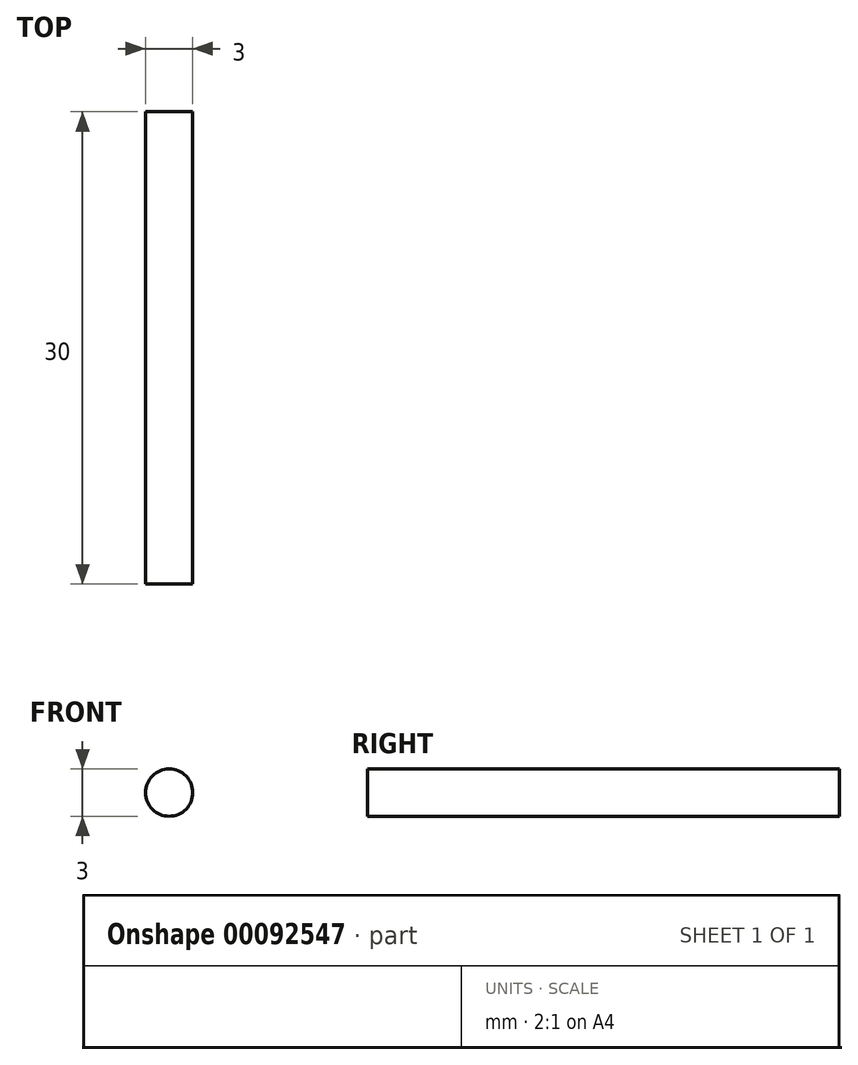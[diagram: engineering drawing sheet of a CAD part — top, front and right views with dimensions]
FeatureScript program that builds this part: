
annotation { "Feature Type Name" : "Feature", "Feature Type Description" : "" }
export const myFeature = defineFeature(function(context is Context, id is Id, definition is map)
    precondition{}
    {
        {
            var Q0;
            Q0=qCreatedBy(makeId("Front.planeOp"),FACE);
            var sketch = newSketch(context, id + "F0", { "sketchPlane" : qUnion([Q0])});
            skCircle(sketch, "E0", {"center": v(-2.3, 5.4) * mm, "radius": 1.5 * mm});
            skSolve(sketch);
        }
        {
            var Q0;
            Q0 = qSketchRegion(id + "F0", true);
            extrude(context, id + "F1", {"entities" : qUnion([Q0]), "depth" : 30 * mm});
        }
    });
